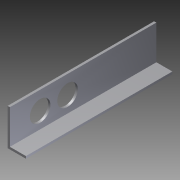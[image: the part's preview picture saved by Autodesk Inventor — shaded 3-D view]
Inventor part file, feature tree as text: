
AUTODESK INVENTOR PART (.ipt)
format: ipt  version: 2012 (Build 160160000, 160)  size: 90,112 bytes
history: native  units: in
note: dims shown in document units (in); Inventor stores cm internally (conversion verified against a paired STEP export)
features: extrude x2, sketch x2
ambient origin geometry x8: Origin, YZ Plane, XZ Plane, XY Plane, X Axis, Y Axis, Z Axis, Center Point
bodies: Solid1 (feature_tree)
feature tree (4):
  extrude  "Extrusion1"  Depth=1.0in
  extrude  "Extrusion2"  Depth=0.125in
  sketch  "Sketch1"  dims[d0=2.0in d1=1.0in]
  sketch  "Sketch2"  dims[d2=0.125in d3=0.125in d4=8.0in d5=0.0in d6=1.125in d7=1.125in d8=1.0in d9=1.65in d10=1.5in d11=8.0in d12=0.0in]
